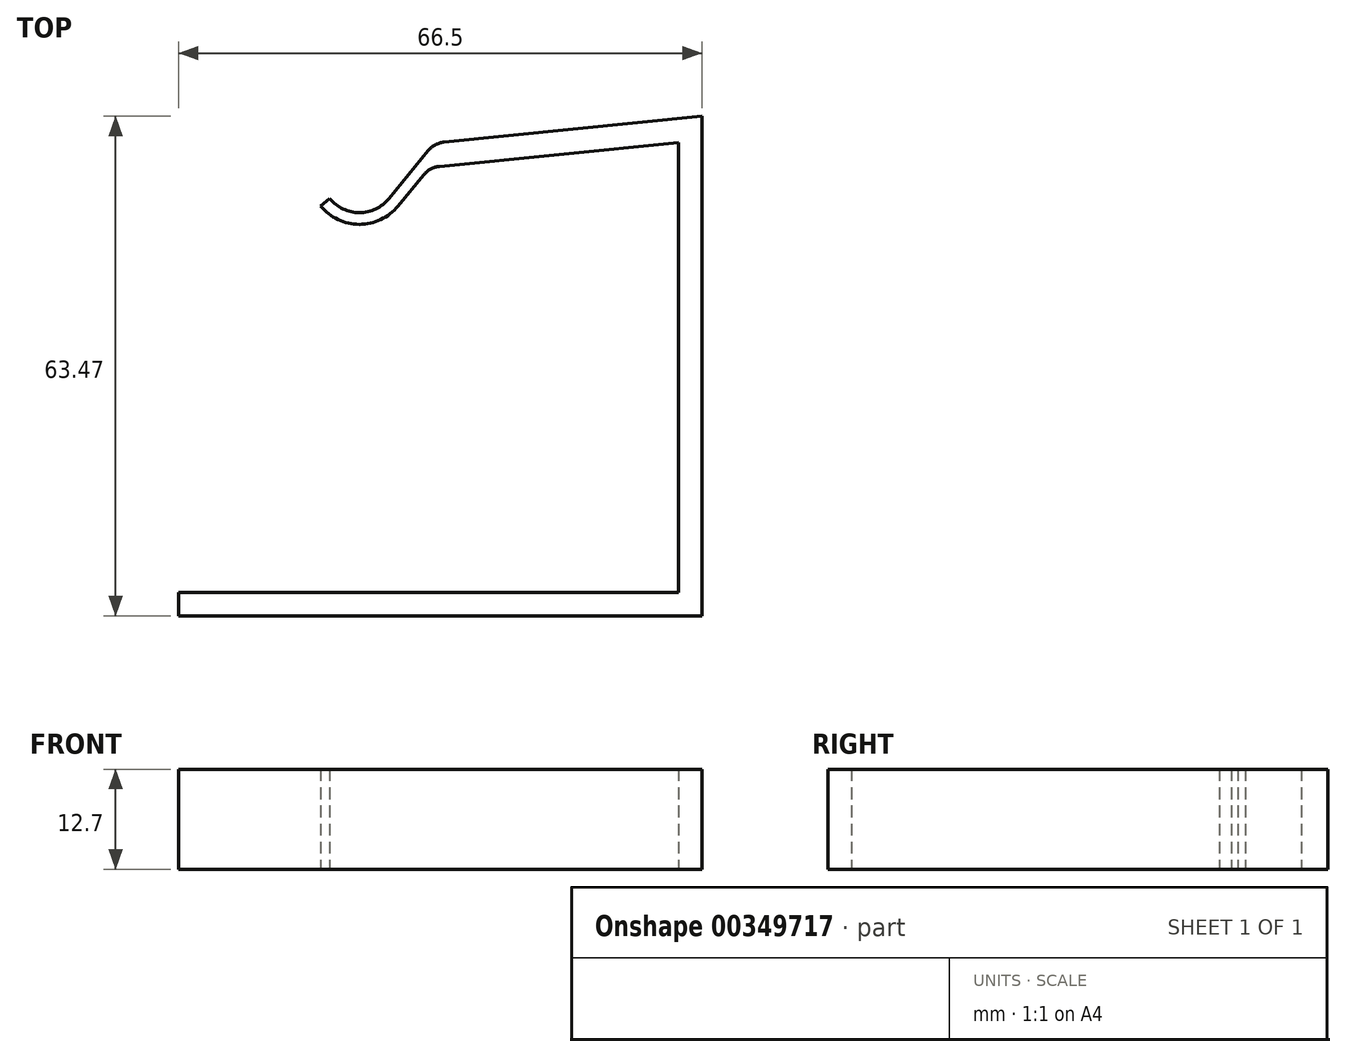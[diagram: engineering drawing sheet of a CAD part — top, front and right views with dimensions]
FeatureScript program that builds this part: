
annotation { "Feature Type Name" : "Feature", "Feature Type Description" : "" }
export const myFeature = defineFeature(function(context is Context, id is Id, definition is map)
    precondition{}
    {
        {
            var Q0;
            Q0=qCreatedBy(makeId("Top.planeOp"),FACE);
            var sketch = newSketch(context, id + "F0", { "sketchPlane" : qUnion([Q0])});
            skLineSegment(sketch, "E0", {"start": v(0, 0) * mm, "end": v(63.5, 0) * mm});
            skLineSegment(sketch, "E1", {"start": v(63.5, 0) * mm, "end": v(63.5, 57.15) * mm});
            skLineSegment(sketch, "E2", {"start": v(63.5, 57.15) * mm, "end": v(31.9, 53.98) * mm});
            skLineSegment(sketch, "E3", {"start": v(31.9, 53.98) * mm, "end": v(27.9, 49.06) * mm});
            skArc(sketch, "E4", {"start": v(27.9, 49.06) * mm, "mid": v(22.97, 46.73) * mm, "end": v(18.06, 49.06) * mm});
            skLineSegment(sketch, "E5.0", {"start": v(66.5, 60.47) * mm, "end": v(32.48, 57.05) * mm});
            skLineSegment(sketch, "E5.1", {"start": v(66.5, -3) * mm, "end": v(66.5, 60.47) * mm});
            skLineSegment(sketch, "E5.2", {"start": v(0, -3) * mm, "end": v(66.5, -3) * mm});
            skLineSegment(sketch, "E6", {"start": v(0, 0) * mm, "end": v(0, -3) * mm});
            skArc(sketch, "E7.0", {"start": v(26.73, 50) * mm, "mid": v(22.97, 48.23) * mm, "end": v(19.22, 50) * mm});
            skLineSegment(sketch, "E7.1", {"start": v(32.48, 57.05) * mm, "end": v(26.73, 50) * mm});
            skLineSegment(sketch, "E8", {"start": v(18.06, 49.06) * mm, "end": v(19.22, 50) * mm});
            skSolve(sketch);
        }
        {
            var Q0;
            Q0=makeQuery(id+"F0.imprint","IMPRINT",FACE,{"disambiguationData":[TD([[makeQuery(id+"F0.imprint","IMPRINT",EDGE,{"derivedFrom":sQuery(id+"F0.wireOp",EDGE,"E0")}),-1.0]])]});
            extrude(context, id + "F1", {"entities" : qUnion([Q0]), "depth" : 12.7 * mm, "offsetDistance" : 25 * mm});
        }
        {
            var Q0;
            Q0=makeQuery(id+"F1.opExtrude","SWEPT_EDGE",EDGE,{"disambiguationData":[OSD([sQuery(id+"F0.wireOp",EDGE,"E2"),sQuery(id+"F0.wireOp",EDGE,"E3")])]});
            var Q1;
            Q1=makeQuery(id+"F1.opExtrude","SWEPT_EDGE",EDGE,{"disambiguationData":[OSD([sQuery(id+"F0.wireOp",EDGE,"E5.0"),sQuery(id+"F0.wireOp",EDGE,"E7.1")])]});
            fillet(context, id + "F2", {"entities" : qUnion([Q0, Q1]), "radius" : 3 * mm, "tangentPropagation" : true, "allowEdgeOverflow" : false});
        }
    });
